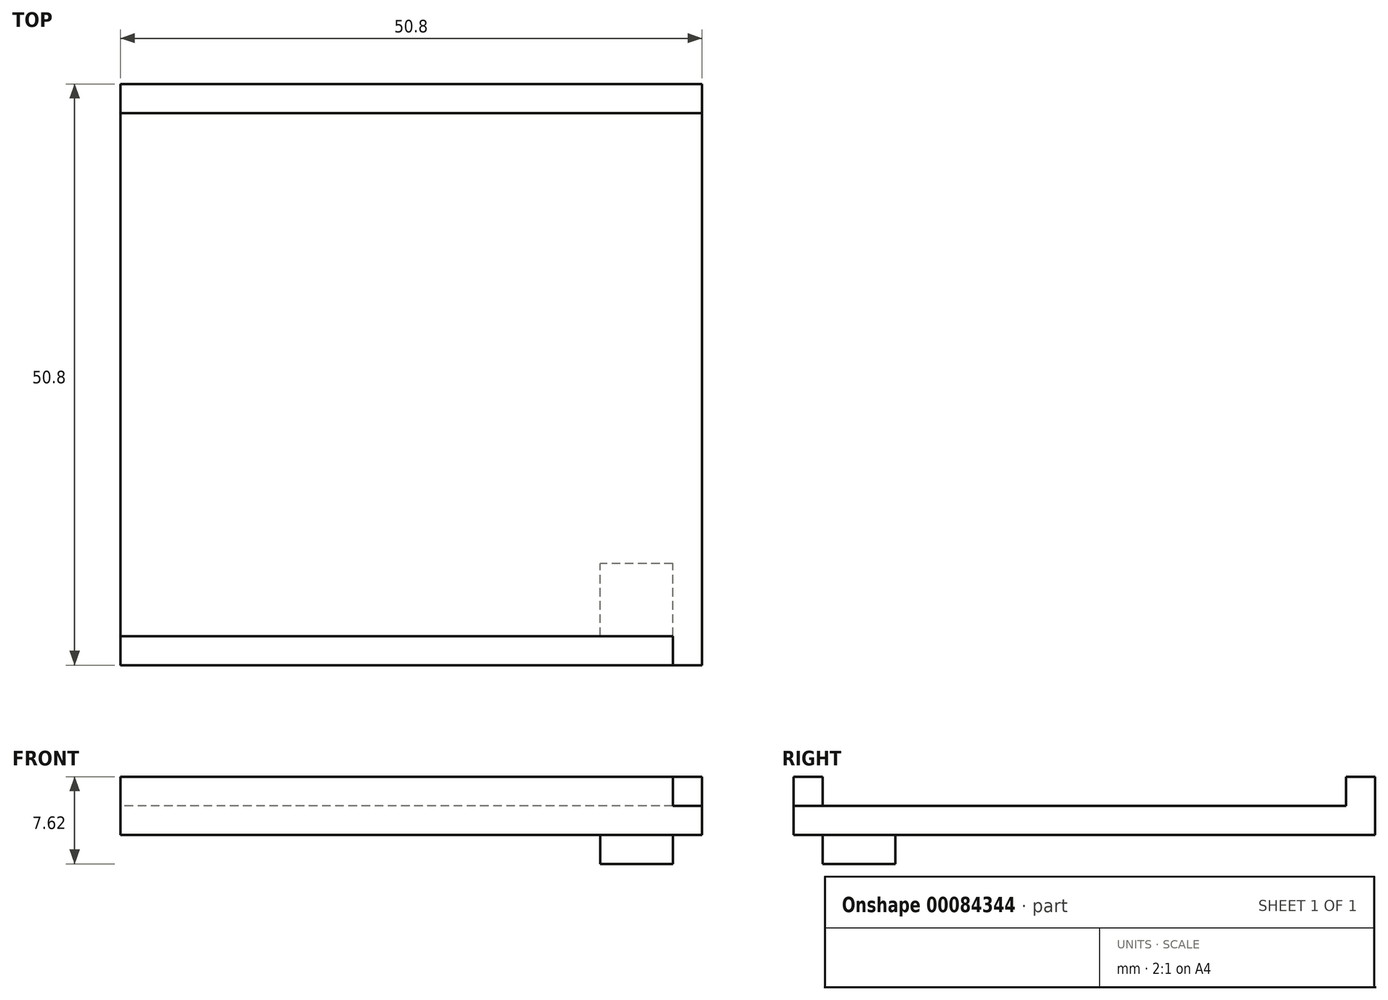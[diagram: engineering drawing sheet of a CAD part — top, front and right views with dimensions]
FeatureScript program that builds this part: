
annotation { "Feature Type Name" : "Feature", "Feature Type Description" : "" }
export const myFeature = defineFeature(function(context is Context, id is Id, definition is map)
    precondition{}
    {
        {
            var Q0;
            Q0=qCreatedBy(makeId("Top.planeOp"),FACE);
            var sketch = newSketch(context, id + "F0", { "sketchPlane" : qUnion([Q0])});
            skLineSegment(sketch, "E0.bottom", {"start": v(25.4, 25.4) * mm, "end": v(-25.4, 25.4) * mm});
            skLineSegment(sketch, "E0.top", {"start": v(25.4, -25.4) * mm, "end": v(-25.4, -25.4) * mm});
            skLineSegment(sketch, "E0.left", {"start": v(25.4, 25.4) * mm, "end": v(25.4, -25.4) * mm});
            skLineSegment(sketch, "E0.right", {"start": v(-25.4, 25.4) * mm, "end": v(-25.4, -25.4) * mm});
            skPoint(sketch, "E0.middle", {"position": v(0, 0) * mm});
            skSolve(sketch);
        }
        {
            var Q0;
            Q0=makeQuery(id+"F0.imprint","IMPRINT",FACE,{"disambiguationData":[TD([[makeQuery(id+"F0.imprint","IMPRINT",EDGE,{"derivedFrom":sQuery(id+"F0.wireOp",EDGE,"E0.bottom")}),1.0]])]});
            extrude(context, id + "F1", {"entities" : qUnion([Q0]), "depth" : 2.54 * mm});
        }
        {
            var Q0;
            Q0=makeQuery(id+"F1.opExtrude","CAP_FACE",FACE,{"disambiguationData":[OSD([sQuery(id+"F0.wireOp",EDGE,"E0.bottom"),sQuery(id+"F0.wireOp",EDGE,"E0.top"),sQuery(id+"F0.wireOp",EDGE,"E0.left"),sQuery(id+"F0.wireOp",EDGE,"E0.right")])],"isStart":false});
            var sketch = newSketch(context, id + "F2", { "sketchPlane" : qUnion([Q0])});
            skLineSegment(sketch, "E1.bottom", {"start": v(-25.4, 25.4) * mm, "end": v(25.4, 25.4) * mm});
            skLineSegment(sketch, "E1.top", {"start": v(-25.4, 22.86) * mm, "end": v(25.4, 22.86) * mm});
            skLineSegment(sketch, "E1.left", {"start": v(-25.4, 25.4) * mm, "end": v(-25.4, 22.86) * mm});
            skLineSegment(sketch, "E1.right", {"start": v(25.4, 25.4) * mm, "end": v(25.4, 22.86) * mm});
            skLineSegment(sketch, "E2.bottom", {"start": v(25.4, 22.86) * mm, "end": v(22.86, 22.86) * mm});
            skLineSegment(sketch, "E2.top", {"start": v(25.4, -25.4) * mm, "end": v(22.86, -25.4) * mm});
            skLineSegment(sketch, "E2.left", {"start": v(25.4, 22.86) * mm, "end": v(25.4, -25.4) * mm});
            skLineSegment(sketch, "E2.right", {"start": v(22.86, 22.86) * mm, "end": v(22.86, -25.4) * mm});
            skLineSegment(sketch, "E3.bottom", {"start": v(22.86, -25.4) * mm, "end": v(-25.4, -25.4) * mm});
            skLineSegment(sketch, "E3.top", {"start": v(22.86, -22.86) * mm, "end": v(-25.4, -22.86) * mm});
            skLineSegment(sketch, "E3.left", {"start": v(22.86, -25.4) * mm, "end": v(22.86, -22.86) * mm});
            skLineSegment(sketch, "E3.right", {"start": v(-25.4, -25.4) * mm, "end": v(-25.4, -22.86) * mm});
            skLineSegment(sketch, "E4.bottom", {"start": v(-25.4, -22.86) * mm, "end": v(-22.86, -22.86) * mm});
            skLineSegment(sketch, "E4.top", {"start": v(-25.4, 22.86) * mm, "end": v(-22.86, 22.86) * mm});
            skLineSegment(sketch, "E4.left", {"start": v(-25.4, -22.86) * mm, "end": v(-25.4, 22.86) * mm});
            skLineSegment(sketch, "E4.right", {"start": v(-22.86, -22.86) * mm, "end": v(-22.86, 22.86) * mm});
            skSolve(sketch);
        }
        {
            var Q0;
            Q0=makeQuery(id+"F2.imprint","IMPRINT",FACE,{"disambiguationData":[TD([[makeQuery(id+"F2.imprint","IMPRINT",EDGE,{"derivedFrom":sQuery(id+"F2.wireOp",EDGE,"E4.bottom")}),1.0]])]});
            var Q1;
            Q1=makeQuery(id+"F2.imprint","IMPRINT",FACE,{"disambiguationData":[TD([[makeQuery(id+"F2.imprint","IMPRINT",EDGE,{"derivedFrom":sQuery(id+"F2.wireOp",EDGE,"E1.bottom")}),1.0]])]});
            var Q2;
            Q2=makeQuery(id+"F2.imprint","IMPRINT",FACE,{"disambiguationData":[TD([[makeQuery(id+"F2.imprint","IMPRINT",EDGE,{"derivedFrom":sQuery(id+"F2.wireOp",EDGE,"E2.bottom")}),1.0]])]});
            var Q3;
            Q3=makeQuery(id+"F2.imprint","IMPRINT",FACE,{"disambiguationData":[TD([[makeQuery(id+"F2.imprint","IMPRINT",EDGE,{"derivedFrom":sQuery(id+"F2.wireOp",EDGE,"E3.bottom")}),-1.0]])]});
            extrude(context, id + "F3", {"entities" : qUnion([Q0, Q1, Q2, Q3]), "operationType" : NewBodyOperationType.ADD, "depth" : 2.54 * mm});
        }
        {
            var Q0;
            Q0=makeQuery(id+"F1.opExtrude","CAP_FACE",FACE,{"disambiguationData":[OSD([sQuery(id+"F0.wireOp",EDGE,"E0.bottom"),sQuery(id+"F0.wireOp",EDGE,"E0.top"),sQuery(id+"F0.wireOp",EDGE,"E0.left"),sQuery(id+"F0.wireOp",EDGE,"E0.right")])],"isStart":true});
            var sketch = newSketch(context, id + "F4", { "sketchPlane" : qUnion([Q0])});
            skLineSegment(sketch, "E5.bottom", {"start": v(25.4, 25.4) * mm, "end": v(22.86, 25.4) * mm});
            skLineSegment(sketch, "E5.top", {"start": v(25.4, 22.86) * mm, "end": v(22.86, 22.86) * mm});
            skLineSegment(sketch, "E5.left", {"start": v(25.4, 25.4) * mm, "end": v(25.4, 22.86) * mm});
            skLineSegment(sketch, "E5.right", {"start": v(22.86, 25.4) * mm, "end": v(22.86, 22.86) * mm});
            skLineSegment(sketch, "E6.bottom", {"start": v(22.86, 22.86) * mm, "end": v(16.5, 22.86) * mm});
            skLineSegment(sketch, "E6.top", {"start": v(22.86, 16.5) * mm, "end": v(16.5, 16.5) * mm});
            skLineSegment(sketch, "E6.left", {"start": v(22.86, 22.86) * mm, "end": v(22.86, 16.5) * mm});
            skLineSegment(sketch, "E6.right", {"start": v(16.5, 22.86) * mm, "end": v(16.5, 16.5) * mm});
            skSolve(sketch);
        }
        {
            var Q0;
            Q0=makeQuery(id+"F4.imprint","IMPRINT",FACE,{"disambiguationData":[TD([[makeQuery(id+"F4.imprint","IMPRINT",EDGE,{"derivedFrom":sQuery(id+"F4.wireOp",EDGE,"E6.bottom")}),1.0]])]});
            extrude(context, id + "F5", {"entities" : qUnion([Q0]), "operationType" : NewBodyOperationType.ADD, "depth" : 2.54 * mm});
        }
    });
